# Revit family: Plumbing-Fixtures_Accessibility-Professionals-Inc_48x37-Freedom-Easy-Step-Shower-Pan
name_source: partatom
category: Plumbing Fixtures
units: mm (PartAtom-declared; Revit-internal decimal feet)

## family parameters
Always vertical = Yes
Classification Number = 23.45.05.14.11.21
Cut with Voids When Loaded = No
Enable Cutting in Views = No
Maintain Annotation Orientation = No
Part Type = Normal
Room Calculation Point = No
Round Connector Dimension = Use Diameter
Shared = No
Work Plane-Based = No

## types (1)
- 48" x 37" Freedom Easy Step Shower Pan
    Assembly Code = D2010.60
    Default Elevation = 0"
    Depth = 37"
    Description = The 48” x 37" walk in shower pan is specially designed for replacing an existing shower or fitting into a smaller bathroom space. The low 3” curb is easy to step over and can accommodate a shower door if desired. Freedom pre-fabricated shower pans are made with fiberglass with applied acrylic surface, 30-year warranty, made in the USA.
    Drain Diameter = 2"
    Flow = 0 GPM
    Height = 4 1/2"
    Horizontal Drain Offset = 18"
    Interior Depth = 35"
    Interior Width = 46"
    Internal Wall Offset Back = 1"
    Internal Wall Offset Side = 1"
    Keynote = 22 40 00.B5
    Manufacturer = Freedom Showers by Accessibility Professionals Inc.
    Model = APF4836SHPAN
    Product Documentation Link = https://www.freedomshowers.com
    Product Material = Freedom Showers by Accessibility Professionals Inc. - Fiberglass Acrylic - White
    Product Page URL = https://www.freedomshowers.com
    Threshold Height = 3"
    URL = https://www.freedomshowers.com
    Version = 1
    Vertical Drain Offset = 24"
    Width = 48"

## geometry (parser evidence)
native form markers: Sweep x1
no freeform markers — native parametric forms only
